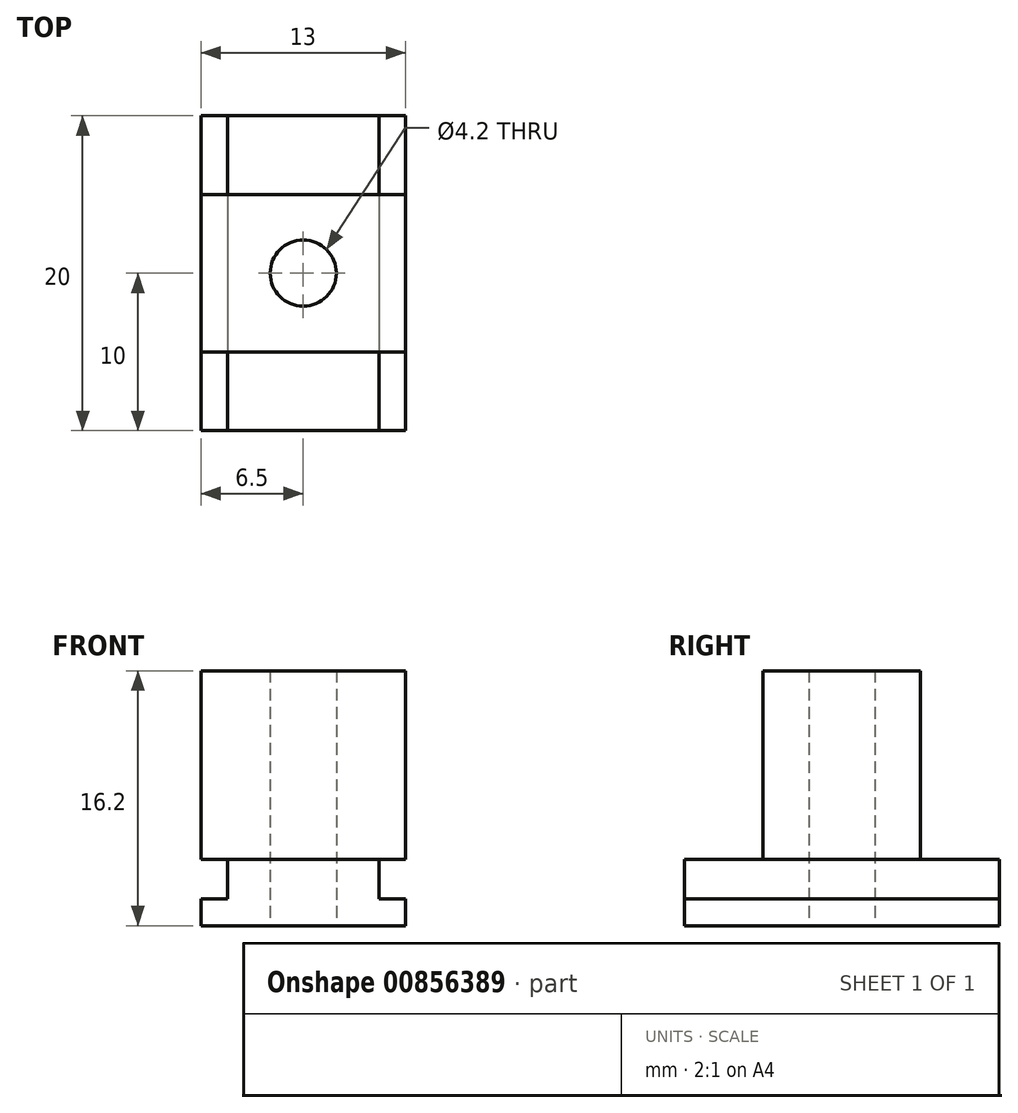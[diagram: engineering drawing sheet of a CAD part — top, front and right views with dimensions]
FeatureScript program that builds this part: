
annotation { "Feature Type Name" : "Feature", "Feature Type Description" : "" }
export const myFeature = defineFeature(function(context is Context, id is Id, definition is map)
    precondition{}
    {
        {
            var Q0;
            Q0=qCreatedBy(makeId("Front.planeOp"),FACE);
            var sketch = newSketch(context, id + "F0", { "sketchPlane" : qUnion([Q0])});
            skLineSegment(sketch, "E0", {"start": v(0, 0) * mm, "end": v(6.5, 0) * mm});
            skLineSegment(sketch, "E1", {"start": v(6.5, 0) * mm, "end": v(6.5, 1.7) * mm});
            skLineSegment(sketch, "E2", {"start": v(6.5, 1.7) * mm, "end": v(4.8, 1.7) * mm});
            skLineSegment(sketch, "E3", {"start": v(4.8, 1.7) * mm, "end": v(4.8, 4.2) * mm});
            skLineSegment(sketch, "E4", {"start": v(4.8, 4.2) * mm, "end": v(0, 4.2) * mm});
            skLineSegment(sketch, "E5.MirrorCS", {"start": v(-4.8, 4.2) * mm, "end": v(0, 4.2) * mm});
            skLineSegment(sketch, "E6.MirrorCS", {"start": v(-4.8, 1.7) * mm, "end": v(-4.8, 4.2) * mm});
            skLineSegment(sketch, "E7.MirrorCS", {"start": v(-6.5, 1.7) * mm, "end": v(-4.8, 1.7) * mm});
            skLineSegment(sketch, "E8.MirrorCS", {"start": v(-6.5, 0) * mm, "end": v(-6.5, 1.7) * mm});
            skLineSegment(sketch, "E9.MirrorCS", {"start": v(0, 0) * mm, "end": v(-6.5, 0) * mm});
            skSolve(sketch);
        }
        {
            var Q0;
            Q0 = qSketchRegion(id + "F0", true);
            extrude(context, id + "F1", {"entities" : qUnion([Q0]), "oppositeDirection" : true, "depth" : 20 * mm, "offsetDistance" : 25 * mm});
        }
        {
            var Q0;
            Q0=qCreatedBy(makeId("Front.planeOp"),FACE);
            cPlane(context, id + "F2", {"entities" : qUnion([Q0]), "cplaneType" : CPlaneType.OFFSET, "offset" : 10 * mm, "oppositeDirection" : true, "width" : 150 * mm, "height" : 150 * mm});
        }
        {
            var Q0;
            Q0=qCreatedBy(id+"F2.planeOp",FACE);
            var sketch = newSketch(context, id + "F3", { "sketchPlane" : qUnion([Q0])});
            skLineSegment(sketch, "E10", {"start": v(-6.5, 4.2) * mm, "end": v(6.5, 4.2) * mm});
            skLineSegment(sketch, "E11", {"start": v(6.5, 4.2) * mm, "end": v(6.5, 16.2) * mm});
            skLineSegment(sketch, "E12", {"start": v(6.5, 16.2) * mm, "end": v(-6.5, 16.2) * mm});
            skLineSegment(sketch, "E13", {"start": v(-6.5, 16.2) * mm, "end": v(-6.5, 4.2) * mm});
            skSolve(sketch);
        }
        {
            var Q0;
            Q0 = qSketchRegion(id + "F3", true);
            extrude(context, id + "F4", {"entities" : qUnion([Q0]), "operationType" : NewBodyOperationType.ADD, "depth" : 5 * mm, "offsetDistance" : 25 * mm, "hasSecondDirection" : true, "secondDirectionOppositeDirection" : true, "secondDirectionDepth" : 5 * mm});
        }
        {
            var Q0;
            Q0=makeQuery(id+"F4.opExtrude","SWEPT_FACE",FACE,{"disambiguationData":[OSD([sQuery(id+"F3.wireOp",EDGE,"E12")])]});
            var sketch = newSketch(context, id + "F5", { "sketchPlane" : qUnion([Q0])});
            skCircle(sketch, "E14", {"center": v(0, 10) * mm, "radius": 2.1 * mm});
            skSolve(sketch);
        }
        {
            var Q0;
            Q0=sQuery(id+"F5.wireOp",VERTEX,"E14.center");
            var Q1;
            Q1=makeQuery(id+"F1.opExtrude","SWEPT_BODY",BODY,{"disambiguationData":[OSD([sQuery(id+"F0.wireOp",EDGE,"E0"),sQuery(id+"F0.wireOp",EDGE,"E1"),sQuery(id+"F0.wireOp",EDGE,"E2"),sQuery(id+"F0.wireOp",EDGE,"E3"),sQuery(id+"F0.wireOp",EDGE,"E4"),sQuery(id+"F0.wireOp",EDGE,"E5.MirrorCS"),sQuery(id+"F0.wireOp",EDGE,"E6.MirrorCS"),sQuery(id+"F0.wireOp",EDGE,"E7.MirrorCS"),sQuery(id+"F0.wireOp",EDGE,"E8.MirrorCS"),sQuery(id+"F0.wireOp",EDGE,"E9.MirrorCS")])]});
            hole(context, id + "F6", {"style" : HoleStyle.SIMPLE, "endStyle" : HoleEndStyle.BLIND, "standardTappedOrClearance" : lookupTablePath({ "standard" : "ISO", "fit" : "Normal", "engagement" : "75%", "pitch" : "0.8 mm", "size" : "M5", "type" : "Tapped" }), "standardBlindInLast" : lookupTablePath({ "fit" : "Standard", "standard" : "ISO", "engagement" : "75%", "pitch" : "0.8 mm", "size" : "M5", "type" : "Tapped" }), "holeDiameter" : 4.2 * mm, "majorDiameter" : 5 * mm, "showTappedDepth" : true, "holeDepth" : 22.4 * mm, "isTappedThrough" : true, "tappedDepth" : 20 * mm, "tapClearance" : 3, "locations" : qUnion([Q0]), "scope" : qUnion([Q1]), "startStyle" : HoleStartStyle.PART});
        }
    });
